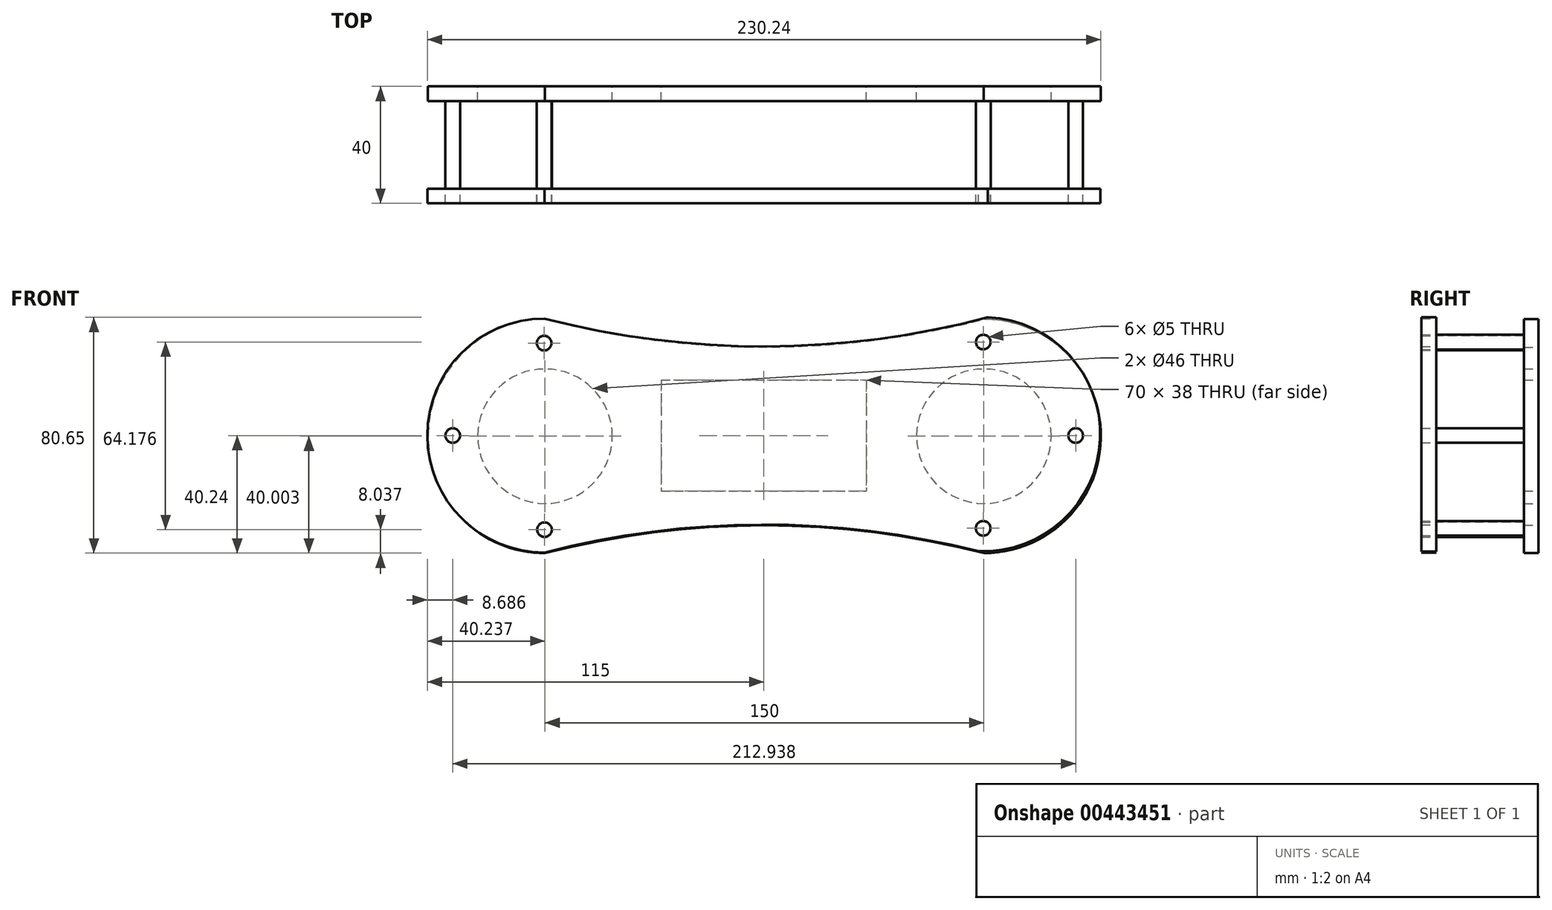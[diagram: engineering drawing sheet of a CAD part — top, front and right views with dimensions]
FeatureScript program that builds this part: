
annotation { "Feature Type Name" : "Feature", "Feature Type Description" : "" }
export const myFeature = defineFeature(function(context is Context, id is Id, definition is map)
    precondition{}
    {
        {
            var Q0;
            Q0=qCreatedBy(makeId("Front.planeOp"),FACE);
            var sketch = newSketch(context, id + "F0", { "sketchPlane" : qUnion([Q0])});
            skArc(sketch, "E0", {"start": v(75.24, -40.24) * mm, "mid": v(115.24, -0.24) * mm, "end": v(75.24, 39.76) * mm});
            skArc(sketch, "E1", {"start": v(-74.76, 39.76) * mm, "mid": v(-114.76, -0.24) * mm, "end": v(-74.76, -40.24) * mm});
            skArc(sketch, "E2", {"start": v(-74.76, 39.76) * mm, "mid": v(0.24, 30.24) * mm, "end": v(75.24, 39.76) * mm});
            skArc(sketch, "E3", {"start": v(75.24, -40.24) * mm, "mid": v(0.24, -30.71) * mm, "end": v(-74.76, -40.24) * mm});
            skCircle(sketch, "E4", {"center": v(75.24, -0.24) * mm, "radius": 23 * mm});
            skCircle(sketch, "E5", {"center": v(-74.76, -0.24) * mm, "radius": 23 * mm});
            skLineSegment(sketch, "E6.bottom", {"start": v(-35, 19) * mm, "end": v(35, 19) * mm});
            skLineSegment(sketch, "E6.top", {"start": v(-35, -19) * mm, "end": v(35, -19) * mm});
            skLineSegment(sketch, "E6.left", {"start": v(-35, 19) * mm, "end": v(-35, -19) * mm});
            skLineSegment(sketch, "E6.right", {"start": v(35, 19) * mm, "end": v(35, -19) * mm});
            skPoint(sketch, "E6.middle", {"position": v(0, 0) * mm});
            skSolve(sketch);
        }
        {
            var Q0;
            Q0=makeQuery(id+"F0.imprint","IMPRINT",FACE,{"disambiguationData":[TD([[makeQuery(id+"F0.imprint","IMPRINT",EDGE,{"derivedFrom":sQuery(id+"F0.wireOp",EDGE,"E0")}),1.0]])]});
            extrude(context, id + "F1", {"entities" : qUnion([Q0]), "depth" : 5 * mm});
        }
        {
            var Q0;
            Q0=qCreatedBy(makeId("Front.planeOp"),FACE);
            cPlane(context, id + "F2", {"entities" : qUnion([Q0]), "cplaneType" : CPlaneType.OFFSET, "offset" : 35 * mm, "width" : 150 * mm, "height" : 150 * mm});
        }
        {
            var Q0;
            Q0=qCreatedBy(id+"F2.planeOp",FACE);
            var sketch = newSketch(context, id + "F3", { "sketchPlane" : qUnion([Q0])});
            skArc(sketch, "E7", {"start": v(73.4, -39.6) * mm, "mid": v(114.98, -1.17) * mm, "end": v(76.56, 40.4) * mm});
            skArc(sketch, "E8", {"start": v(-75, 40) * mm, "mid": v(-115, 0) * mm, "end": v(-75, -40) * mm});
            skArc(sketch, "E9", {"start": v(-75, 40) * mm, "mid": v(0.8, 30.47) * mm, "end": v(76.56, 40.4) * mm});
            skArc(sketch, "E10", {"start": v(73.4, -39.6) * mm, "mid": v(-0.82, -30.47) * mm, "end": v(-75, -40) * mm});
            skCircle(sketch, "E11", {"center": v(75.03, 31.97) * mm, "radius": 2.5 * mm});
            skCircle(sketch, "E12", {"center": v(75, -31.73) * mm, "radius": 2.5 * mm});
            skCircle(sketch, "E13", {"center": v(-75.07, 31.6) * mm, "radius": 2.5 * mm});
            skCircle(sketch, "E14", {"center": v(-74.95, -32.2) * mm, "radius": 2.5 * mm});
            skCircle(sketch, "E15", {"center": v(-106.31, 0) * mm, "radius": 2.5 * mm});
            skCircle(sketch, "E16", {"center": v(106.62, 0) * mm, "radius": 2.5 * mm});
            skSolve(sketch);
        }
        {
            var Q0;
            Q0=qSketchRegion(id+"F3",true);
            extrude(context, id + "F4", {"entities" : qUnion([Q0]), "depth" : 5 * mm});
        }
        {
            var Q0;
            Q0=makeQuery(id+"F3.imprint","IMPRINT",FACE,{"disambiguationData":[TD([[makeQuery(id+"F3.imprint","IMPRINT",EDGE,{"derivedFrom":sQuery(id+"F3.wireOp",EDGE,"E13")}),1.0]])]});
            var Q1;
            Q1=makeQuery(id+"F3.imprint","IMPRINT",FACE,{"disambiguationData":[TD([[makeQuery(id+"F3.imprint","IMPRINT",EDGE,{"derivedFrom":sQuery(id+"F3.wireOp",EDGE,"E15")}),1.0]])]});
            var Q2;
            Q2=makeQuery(id+"F3.imprint","IMPRINT",FACE,{"disambiguationData":[TD([[makeQuery(id+"F3.imprint","IMPRINT",EDGE,{"derivedFrom":sQuery(id+"F3.wireOp",EDGE,"E14")}),1.0]])]});
            var Q3;
            Q3=makeQuery(id+"F3.imprint","IMPRINT",FACE,{"disambiguationData":[TD([[makeQuery(id+"F3.imprint","IMPRINT",EDGE,{"derivedFrom":sQuery(id+"F3.wireOp",EDGE,"E11")}),1.0]])]});
            var Q4;
            Q4=makeQuery(id+"F3.imprint","IMPRINT",FACE,{"disambiguationData":[TD([[makeQuery(id+"F3.imprint","IMPRINT",EDGE,{"derivedFrom":sQuery(id+"F3.wireOp",EDGE,"E16")}),1.0]])]});
            var Q5;
            Q5=makeQuery(id+"F3.imprint","IMPRINT",FACE,{"disambiguationData":[TD([[makeQuery(id+"F3.imprint","IMPRINT",EDGE,{"derivedFrom":sQuery(id+"F3.wireOp",EDGE,"E12")}),1.0]])]});
            extrude(context, id + "F5", {"entities" : qUnion([Q0, Q1, Q2, Q3, Q4, Q5]), "operationType" : NewBodyOperationType.ADD, "oppositeDirection" : true, "depth" : 30 * mm});
        }
    });
